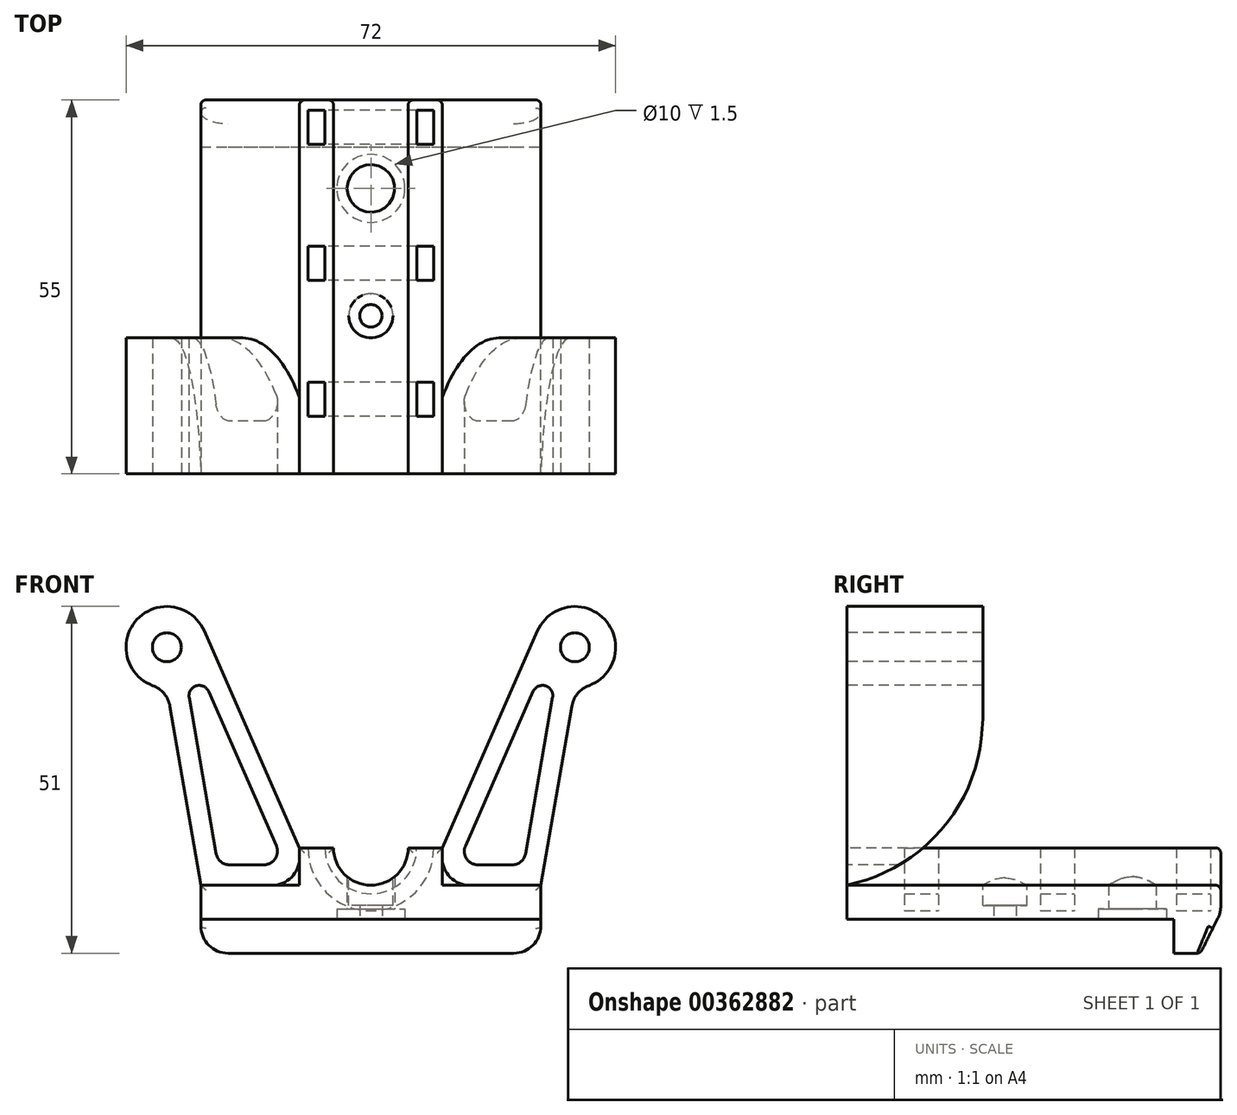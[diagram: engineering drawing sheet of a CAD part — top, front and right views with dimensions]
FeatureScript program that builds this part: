
annotation { "Feature Type Name" : "Feature", "Feature Type Description" : "" }
export const myFeature = defineFeature(function(context is Context, id is Id, definition is map)
    precondition{}
    {
        {
            var Q0;
            Q0=qCreatedBy(makeId("Top.planeOp"),FACE);
            var sketch = newSketch(context, id + "F0", { "sketchPlane" : qUnion([Q0])});
            skCircle(sketch, "E0", {"center": v(0, 0) * mm, "radius": 3.5 * mm});
            skLineSegment(sketch, "E1", {"start": v(0, 0) * mm, "end": v(0, -18.75) * mm, "construction": true});
            skCircle(sketch, "E2", {"center": v(0, -18.75) * mm, "radius": 1.65 * mm});
            skLineSegment(sketch, "E3", {"start": v(0, 0) * mm, "end": v(0, 13) * mm, "construction": true});
            skLineSegment(sketch, "E4", {"start": v(0, 13) * mm, "end": v(-25, 13) * mm});
            skLineSegment(sketch, "E5", {"start": v(-25, 13) * mm, "end": v(-25, -42) * mm});
            skLineSegment(sketch, "E6", {"start": v(-25, -42) * mm, "end": v(25, -42) * mm});
            skLineSegment(sketch, "E7", {"start": v(25, -42) * mm, "end": v(25, 13) * mm});
            skLineSegment(sketch, "E8", {"start": v(25, 13) * mm, "end": v(0, 13) * mm});
            skSolve(sketch);
        }
        {
            var Q0;
            Q0 = qSketchRegion(id + "F0", true);
            extrude(context, id + "F1", {"entities" : qUnion([Q0]), "depth" : 5 * mm});
        }
        {
            var Q0;
            Q0=makeQuery(id+"F1.opExtrude","CAP_FACE",FACE,{"disambiguationData":[OSD([sQuery(id+"F0.wireOp",EDGE,"E0"),sQuery(id+"F0.wireOp",EDGE,"E2"),sQuery(id+"F0.wireOp",EDGE,"E4"),sQuery(id+"F0.wireOp",EDGE,"E5"),sQuery(id+"F0.wireOp",EDGE,"E6"),sQuery(id+"F0.wireOp",EDGE,"E7"),sQuery(id+"F0.wireOp",EDGE,"E8")])],"isStart":true});
            var sketch = newSketch(context, id + "F2", { "sketchPlane" : qUnion([Q0])});
            skLineSegment(sketch, "E9.bottom", {"start": v(-25, -13) * mm, "end": v(25, -13) * mm});
            skLineSegment(sketch, "E9.top", {"start": v(-25, -6.1) * mm, "end": v(25, -6.1) * mm});
            skLineSegment(sketch, "E9.left", {"start": v(-25, -13) * mm, "end": v(-25, -6.1) * mm});
            skLineSegment(sketch, "E9.right", {"start": v(25, -13) * mm, "end": v(25, -6.1) * mm});
            skSolve(sketch);
        }
        {
            var Q0;
            Q0 = qSketchRegion(id + "F2", true);
            extrude(context, id + "F3", {"entities" : qUnion([Q0]), "operationType" : NewBodyOperationType.ADD, "depth" : 5 * mm});
        }
        {
            var Q0;
            Q0=makeQuery(id+"F1.opExtrude","CAP_FACE",FACE,{"disambiguationData":[OSD([sQuery(id+"F0.wireOp",EDGE,"E0"),sQuery(id+"F0.wireOp",EDGE,"E2"),sQuery(id+"F0.wireOp",EDGE,"E4"),sQuery(id+"F0.wireOp",EDGE,"E5"),sQuery(id+"F0.wireOp",EDGE,"E6"),sQuery(id+"F0.wireOp",EDGE,"E7"),sQuery(id+"F0.wireOp",EDGE,"E8")])],"isStart":true});
            var sketch = newSketch(context, id + "F4", { "sketchPlane" : qUnion([Q0])});
            skCircle(sketch, "E10", {"center": v(0, 0) * mm, "radius": 5 * mm});
            skSolve(sketch);
        }
        {
            var Q0;
            Q0 = qSketchRegion(id + "F4", true);
            extrude(context, id + "F5", {"entities" : qUnion([Q0]), "operationType" : NewBodyOperationType.REMOVE, "oppositeDirection" : true, "depth" : 1.5 * mm});
        }
        {
            var Q0;
            Q0=makeQuery(id+"F1.opExtrude","CAP_FACE",FACE,{"disambiguationData":[OSD([sQuery(id+"F0.wireOp",EDGE,"E0"),sQuery(id+"F0.wireOp",EDGE,"E2"),sQuery(id+"F0.wireOp",EDGE,"E4"),sQuery(id+"F0.wireOp",EDGE,"E5"),sQuery(id+"F0.wireOp",EDGE,"E6"),sQuery(id+"F0.wireOp",EDGE,"E7"),sQuery(id+"F0.wireOp",EDGE,"E8")])],"isStart":false});
            var sketch = newSketch(context, id + "F6", { "sketchPlane" : qUnion([Q0])});
            skCircle(sketch, "E11", {"center": v(0, -18.75) * mm, "radius": 3.25 * mm});
            skSolve(sketch);
        }
        {
            var Q0;
            Q0 = qSketchRegion(id + "F6", true);
            extrude(context, id + "F7", {"entities" : qUnion([Q0]), "operationType" : NewBodyOperationType.REMOVE, "oppositeDirection" : true, "depth" : 3 * mm});
        }
        {
            var Q0;
            Q0=makeQuery(id+"F3.opExtrude","CAP_EDGE",EDGE,{"disambiguationData":[OSD([sQuery(id+"F2.wireOp",EDGE,"E9.bottom")])],"isStart":false});
            chamfer(context, id + "F8", {"entities" : qUnion([Q0]), "chamferType" : ChamferType.TWO_OFFSETS, "width1" : 6 * mm, "oppositeDirection" : false, "width2" : 3 * mm, "tangentPropagation" : true});
        }
        {
            var Q0;
            Q0=makeQuery(id+"F1.opExtrude","SWEPT_FACE",FACE,{"disambiguationData":[OSD([sQuery(id+"F0.wireOp",EDGE,"E6")])]});
            var sketch = newSketch(context, id + "F9", { "sketchPlane" : qUnion([Q0])});
            skLineSegment(sketch, "E12", {"start": v(0, 0) * mm, "end": v(0, 10.5) * mm, "construction": true});
            skPoint(sketch, "E12.endSnap0", {"position": v(0, 5) * mm});
            skArc(sketch, "E13", {"start": v(-5.5, 10.5) * mm, "mid": v(0, 5) * mm, "end": v(5.5, 10.5) * mm});
            skLineSegment(sketch, "E14", {"start": v(-5.5, 10.5) * mm, "end": v(-10.5, 10.5) * mm});
            skLineSegment(sketch, "E15", {"start": v(-10.5, 10.5) * mm, "end": v(-10.5, 4.5) * mm});
            skLineSegment(sketch, "E16", {"start": v(5.5, 10.5) * mm, "end": v(10.5, 10.5) * mm});
            skLineSegment(sketch, "E17", {"start": v(10.5, 10.5) * mm, "end": v(10.5, 4.5) * mm});
            skLineSegment(sketch, "E18", {"start": v(10.5, 4.5) * mm, "end": v(-10.5, 4.5) * mm});
            skSolve(sketch);
        }
        {
            var Q0;
            Q0 = qSketchRegion(id + "F9", true);
            extrude(context, id + "F10", {"entities" : qUnion([Q0]), "operationType" : NewBodyOperationType.ADD, "oppositeDirection" : true, "depth" : 55 * mm});
        }
        {
            var Q0;
            Q0=makeQuery(id+"F10.boolean.opBoolean","MERGE",FACE,{"derivedFrom":[makeQuery(id+"F1.opExtrude","SWEPT_FACE",FACE,{"disambiguationData":[OSD([sQuery(id+"F0.wireOp",EDGE,"E6")])]}),makeQuery(id+"F10.opExtrude","CAP_FACE",FACE,{"disambiguationData":[OSD([sQuery(id+"F9.wireOp",EDGE,"E13"),sQuery(id+"F9.wireOp",EDGE,"E14"),sQuery(id+"F9.wireOp",EDGE,"E15"),sQuery(id+"F9.wireOp",EDGE,"E16"),sQuery(id+"F9.wireOp",EDGE,"E17"),sQuery(id+"F9.wireOp",EDGE,"E18")])],"isStart":true})]});
            var sketch = newSketch(context, id + "F11", { "sketchPlane" : qUnion([Q0])});
            skLineSegment(sketch, "E19", {"start": v(0, 0) * mm, "end": v(0, 40) * mm, "construction": true});
            skPoint(sketch, "E19.endSnap0", {"position": v(0, 5) * mm});
            skLineSegment(sketch, "E20", {"start": v(0, 40) * mm, "end": v(-30, 40) * mm, "construction": true});
            skLineSegment(sketch, "E21", {"start": v(0, 40) * mm, "end": v(30, 40) * mm, "construction": true});
            skCircle(sketch, "E22", {"center": v(-30, 40) * mm, "radius": 2.12 * mm});
            skCircle(sketch, "E23", {"center": v(30, 40) * mm, "radius": 2.12 * mm});
            skArc(sketch, "E24", {"start": v(-24.5, 42.41) * mm, "mid": v(-35.02, 43.28) * mm, "end": v(-30, 34) * mm});
            skArc(sketch, "E25", {"start": v(30, 34) * mm, "mid": v(35.02, 43.28) * mm, "end": v(24.5, 42.41) * mm});
            skLineSegment(sketch, "E26", {"start": v(-30, 34) * mm, "end": v(-25, 5) * mm});
            skLineSegment(sketch, "E27", {"start": v(-10.5, 10.5) * mm, "end": v(-24.5, 42.41) * mm});
            skLineSegment(sketch, "E28", {"start": v(-25, 5) * mm, "end": v(-10.5, 5) * mm});
            skLineSegment(sketch, "E29", {"start": v(-10.5, 5) * mm, "end": v(-10.5, 10.5) * mm});
            skLineSegment(sketch, "E30.0", {"start": v(-13.9, 10.8) * mm, "end": v(-23.87, 33.5) * mm});
            skLineSegment(sketch, "E30.1", {"start": v(-20.79, 8) * mm, "end": v(-15.74, 8) * mm});
            skLineSegment(sketch, "E30.2", {"start": v(-26.72, 32.64) * mm, "end": v(-22.76, 9.66) * mm});
            skPoint(sketch, "E31.visualSharp", {"position": v(-22.47, 8) * mm});
            skArc(sketch, "E31.filletArc", {"start": v(-22.76, 9.66) * mm, "mid": v(-22.08, 8.47) * mm, "end": v(-20.79, 8) * mm});
            skPoint(sketch, "E32.visualSharp", {"position": v(-12.68, 8) * mm});
            skArc(sketch, "E32.filletArc", {"start": v(-15.74, 8) * mm, "mid": v(-14.07, 8.9) * mm, "end": v(-13.9, 10.8) * mm});
            skPoint(sketch, "E33.visualSharp", {"position": v(-28.8, 44.75) * mm});
            skArc(sketch, "E33.filletArc", {"start": v(-23.87, 33.5) * mm, "mid": v(-25.67, 34.33) * mm, "end": v(-26.72, 32.64) * mm});
            skLineSegment(sketch, "E34.MirrorCS", {"start": v(13.9, 10.8) * mm, "end": v(23.87, 33.5) * mm});
            skLineSegment(sketch, "E35.MirrorCS", {"start": v(10.5, 10.5) * mm, "end": v(24.5, 42.41) * mm});
            skLineSegment(sketch, "E36.MirrorCS", {"start": v(10.5, 5) * mm, "end": v(10.5, 10.5) * mm});
            skLineSegment(sketch, "E37.MirrorCS", {"start": v(25, 5) * mm, "end": v(10.5, 5) * mm});
            skLineSegment(sketch, "E38.MirrorCS", {"start": v(30, 34) * mm, "end": v(25, 5) * mm});
            skArc(sketch, "E39.MirrorCS", {"start": v(15.74, 8) * mm, "mid": v(14.07, 8.9) * mm, "end": v(13.9, 10.8) * mm});
            skLineSegment(sketch, "E40.MirrorCS", {"start": v(20.79, 8) * mm, "end": v(15.74, 8) * mm});
            skArc(sketch, "E41.MirrorCS", {"start": v(22.76, 9.66) * mm, "mid": v(22.08, 8.47) * mm, "end": v(20.79, 8) * mm});
            skLineSegment(sketch, "E42.MirrorCS", {"start": v(26.72, 32.64) * mm, "end": v(22.76, 9.66) * mm});
            skArc(sketch, "E43.MirrorCS", {"start": v(23.87, 33.5) * mm, "mid": v(25.67, 34.33) * mm, "end": v(26.72, 32.64) * mm});
            skSolve(sketch);
        }
        {
            var Q0;
            Q0=makeQuery(id+"F10.opExtrude","SWEPT_FACE",FACE,{"disambiguationData":[OSD([sQuery(id+"F9.wireOp",EDGE,"E16")])]});
            var sketch = newSketch(context, id + "F12", { "sketchPlane" : qUnion([Q0])});
            skLineSegment(sketch, "E44", {"start": v(0, 0) * mm, "end": v(0, 13) * mm, "construction": true});
            skLineSegment(sketch, "E45", {"start": v(0, 13) * mm, "end": v(8, 13) * mm, "construction": true});
            skLineSegment(sketch, "E46", {"start": v(8, 13) * mm, "end": v(8, -42) * mm, "construction": true});
            skLineSegment(sketch, "E47.bottom", {"start": v(9.25, -33.5) * mm, "end": v(6.75, -33.5) * mm});
            skLineSegment(sketch, "E47.top", {"start": v(9.25, -28.5) * mm, "end": v(6.75, -28.5) * mm});
            skLineSegment(sketch, "E47.left", {"start": v(9.25, -33.5) * mm, "end": v(9.25, -28.5) * mm});
            skLineSegment(sketch, "E47.right", {"start": v(6.75, -33.5) * mm, "end": v(6.75, -28.5) * mm});
            skPoint(sketch, "E47.middle", {"position": v(8, -31) * mm});
            skLineSegment(sketch, "E48.bottom", {"start": v(9.25, 6.5) * mm, "end": v(6.75, 6.5) * mm});
            skLineSegment(sketch, "E48.top", {"start": v(9.25, 11.5) * mm, "end": v(6.75, 11.5) * mm});
            skLineSegment(sketch, "E48.left", {"start": v(9.25, 6.5) * mm, "end": v(9.25, 11.5) * mm});
            skLineSegment(sketch, "E48.right", {"start": v(6.75, 6.5) * mm, "end": v(6.75, 11.5) * mm});
            skPoint(sketch, "E48.middle", {"position": v(8, 9) * mm});
            skLineSegment(sketch, "E49.bottom", {"start": v(9.25, -13.5) * mm, "end": v(6.75, -13.5) * mm});
            skLineSegment(sketch, "E49.top", {"start": v(9.25, -8.5) * mm, "end": v(6.75, -8.5) * mm});
            skLineSegment(sketch, "E49.left", {"start": v(9.25, -13.5) * mm, "end": v(9.25, -8.5) * mm});
            skLineSegment(sketch, "E49.right", {"start": v(6.75, -13.5) * mm, "end": v(6.75, -8.5) * mm});
            skPoint(sketch, "E49.middle", {"position": v(8, -11) * mm});
            skSolve(sketch);
        }
        {
            var Q0;
            Q0 = qSketchRegion(id + "F12", true);
            var Q1;
            Q1=sQuery(id+"F12.wireOp",EDGE,"E44");
            revolve(context, id + "F13", {"operationType" : NewBodyOperationType.REMOVE, "entities" : qUnion([Q0]), "axis" : qUnion([Q1]), "revolveType" : RevolveType.FULL, "oppositeDirection" : true});
        }
        {
            var Q0;
            Q0 = qSketchRegion(id + "F11", true);
            extrude(context, id + "F14", {"entities" : qUnion([Q0]), "oppositeDirection" : true, "depth" : 20 * mm});
        }
        {
            var Q0;
            Q0=makeQuery(id+"F10.boolean.opBoolean","INTERSECT",EDGE,{"derivedFrom":[makeQuery(id+"F1.opExtrude","CAP_FACE",FACE,{"disambiguationData":[OSD([sQuery(id+"F0.wireOp",EDGE,"E0"),sQuery(id+"F0.wireOp",EDGE,"E2"),sQuery(id+"F0.wireOp",EDGE,"E4"),sQuery(id+"F0.wireOp",EDGE,"E5"),sQuery(id+"F0.wireOp",EDGE,"E6"),sQuery(id+"F0.wireOp",EDGE,"E7"),sQuery(id+"F0.wireOp",EDGE,"E8")])],"isStart":false}),makeQuery(id+"F10.opExtrude","SWEPT_FACE",FACE,{"disambiguationData":[OSD([sQuery(id+"F9.wireOp",EDGE,"E15")])]})]});
            var Q1;
            Q1=makeQuery(id+"F10.boolean.opBoolean","INTERSECT",EDGE,{"derivedFrom":[makeQuery(id+"F1.opExtrude","CAP_FACE",FACE,{"disambiguationData":[OSD([sQuery(id+"F0.wireOp",EDGE,"E0"),sQuery(id+"F0.wireOp",EDGE,"E2"),sQuery(id+"F0.wireOp",EDGE,"E4"),sQuery(id+"F0.wireOp",EDGE,"E5"),sQuery(id+"F0.wireOp",EDGE,"E6"),sQuery(id+"F0.wireOp",EDGE,"E7"),sQuery(id+"F0.wireOp",EDGE,"E8")])],"isStart":false}),makeQuery(id+"F10.opExtrude","SWEPT_FACE",FACE,{"disambiguationData":[OSD([sQuery(id+"F9.wireOp",EDGE,"E17")])]})]});
            var Q2;
            Q2=makeQuery(id+"F3.opExtrude","CAP_EDGE",EDGE,{"disambiguationData":[OSD([sQuery(id+"F2.wireOp",EDGE,"E9.right")])],"isStart":false});
            var Q3;
            Q3=makeQuery(id+"F3.opExtrude","CAP_EDGE",EDGE,{"disambiguationData":[OSD([sQuery(id+"F2.wireOp",EDGE,"E9.left")])],"isStart":false});
            var Q4;
            {var subQ0=sQuery(id+"F2.wireOp",EDGE,"E9.bottom");Q4=makeQuery(id+"F8.opChamfer","BLEND_EDGE",EDGE,{"blendedFrom":[makeQuery(id+"F3.opExtrude","CAP_EDGE",EDGE,{"disambiguationData":[OSD([subQ0])],"isStart":false}),makeQuery(id+"F3.boolean.opBoolean","MERGE",FACE,{"derivedFrom":[makeQuery(id+"F1.opExtrude","SWEPT_FACE",FACE,{"disambiguationData":[OSD([sQuery(id+"F0.wireOp",EDGE,"E4"),sQuery(id+"F0.wireOp",EDGE,"E8")])]}),makeQuery(id+"F3.opExtrude","SWEPT_FACE",FACE,{"disambiguationData":[OSD([subQ0])]})]})],"blendedInto":[makeQuery(id+"F3.boolean.opBoolean","MERGE",FACE,{"derivedFrom":[makeQuery(id+"F1.opExtrude","SWEPT_FACE",FACE,{"disambiguationData":[OSD([sQuery(id+"F0.wireOp",EDGE,"E4"),sQuery(id+"F0.wireOp",EDGE,"E8")])]}),makeQuery(id+"F3.opExtrude","SWEPT_FACE",FACE,{"disambiguationData":[OSD([subQ0])]})]})]});}
            var Q5;
            Q5=makeQuery(id+"F14.opExtrude","SWEPT_EDGE",EDGE,{"disambiguationData":[OSD([sQuery(id+"F11.wireOp",EDGE,"E25"),sQuery(id+"F11.wireOp",EDGE,"E38.MirrorCS")])]});
            var Q6;
            Q6=makeQuery(id+"F14.opExtrude","SWEPT_EDGE",EDGE,{"disambiguationData":[OSD([sQuery(id+"F11.wireOp",EDGE,"E24"),sQuery(id+"F11.wireOp",EDGE,"E26")])]});
            fillet(context, id + "F15", {"entities" : qUnion([Q0, Q1, Q2, Q3, Q4, Q5, Q6]), "radius" : 4 * mm, "tangentPropagation" : true, "allowEdgeOverflow" : false});
        }
        {
            var Q0;
            Q0=makeQuery(id+"F14.opExtrude","CAP_EDGE",EDGE,{"disambiguationData":[OSD([sQuery(id+"F11.wireOp",EDGE,"E28")])],"isStart":false});
            var Q1;
            Q1=makeQuery(id+"F14.opExtrude","CAP_EDGE",EDGE,{"disambiguationData":[OSD([sQuery(id+"F11.wireOp",EDGE,"E37.MirrorCS")])],"isStart":false});
            fillet(context, id + "F16", {"entities" : qUnion([Q0, Q1]), "radius" : 25 * mm, "tangentPropagation" : true, "allowEdgeOverflow" : false});
        }
        {
            var Q0;
            Q0=makeQuery(id+"F10.opExtrude","CAP_EDGE",EDGE,{"disambiguationData":[OSD([sQuery(id+"F9.wireOp",EDGE,"E14")])],"isStart":false});
            var Q1;
            Q1=makeQuery(id+"F10.opExtrude","CAP_EDGE",EDGE,{"disambiguationData":[OSD([sQuery(id+"F9.wireOp",EDGE,"E13")])],"isStart":false});
            var Q2;
            Q2=makeQuery(id+"F10.opExtrude","CAP_EDGE",EDGE,{"disambiguationData":[OSD([sQuery(id+"F9.wireOp",EDGE,"E16")])],"isStart":false});
            var Q3;
            {var subQ0=sQuery(id+"F9.wireOp",EDGE,"E17");var subQ1=sQuery(id+"F0.wireOp",EDGE,"E8");var subQ2=sQuery(id+"F0.wireOp",EDGE,"E4");Q3=makeQuery(id+"F15.opFillet","BLEND_EDGE",EDGE,{"blendedFrom":[makeQuery(id+"F10.boolean.opBoolean","INTERSECT",EDGE,{"derivedFrom":[makeQuery(id+"F1.opExtrude","CAP_FACE",FACE,{"disambiguationData":[OSD([sQuery(id+"F0.wireOp",EDGE,"E0"),sQuery(id+"F0.wireOp",EDGE,"E2"),subQ2,sQuery(id+"F0.wireOp",EDGE,"E5"),sQuery(id+"F0.wireOp",EDGE,"E6"),sQuery(id+"F0.wireOp",EDGE,"E7"),subQ1])],"isStart":false}),makeQuery(id+"F10.opExtrude","SWEPT_FACE",FACE,{"disambiguationData":[OSD([subQ0])]})]}),makeQuery(id+"F10.boolean.opBoolean","MERGE",FACE,{"derivedFrom":[makeQuery(id+"F3.boolean.opBoolean","MERGE",FACE,{"derivedFrom":[makeQuery(id+"F1.opExtrude","SWEPT_FACE",FACE,{"disambiguationData":[OSD([subQ2,subQ1])]}),makeQuery(id+"F3.opExtrude","SWEPT_FACE",FACE,{"disambiguationData":[OSD([sQuery(id+"F2.wireOp",EDGE,"E9.bottom")])]})]}),makeQuery(id+"F10.opExtrude","CAP_FACE",FACE,{"disambiguationData":[OSD([sQuery(id+"F9.wireOp",EDGE,"E13"),sQuery(id+"F9.wireOp",EDGE,"E14"),sQuery(id+"F9.wireOp",EDGE,"E15"),sQuery(id+"F9.wireOp",EDGE,"E16"),subQ0,sQuery(id+"F9.wireOp",EDGE,"E18")])],"isStart":false})]})],"blendedInto":[makeQuery(id+"F10.boolean.opBoolean","MERGE",FACE,{"derivedFrom":[makeQuery(id+"F3.boolean.opBoolean","MERGE",FACE,{"derivedFrom":[makeQuery(id+"F1.opExtrude","SWEPT_FACE",FACE,{"disambiguationData":[OSD([subQ2,subQ1])]}),makeQuery(id+"F3.opExtrude","SWEPT_FACE",FACE,{"disambiguationData":[OSD([sQuery(id+"F2.wireOp",EDGE,"E9.bottom")])]})]}),makeQuery(id+"F10.opExtrude","CAP_FACE",FACE,{"disambiguationData":[OSD([sQuery(id+"F9.wireOp",EDGE,"E13"),sQuery(id+"F9.wireOp",EDGE,"E14"),sQuery(id+"F9.wireOp",EDGE,"E15"),sQuery(id+"F9.wireOp",EDGE,"E16"),subQ0,sQuery(id+"F9.wireOp",EDGE,"E18")])],"isStart":false})]})]});}
            var Q4;
            {var subQ0=sQuery(id+"F9.wireOp",EDGE,"E15");var subQ1=sQuery(id+"F0.wireOp",EDGE,"E8");var subQ2=sQuery(id+"F0.wireOp",EDGE,"E4");Q4=makeQuery(id+"F15.opFillet","BLEND_EDGE",EDGE,{"blendedFrom":[makeQuery(id+"F10.boolean.opBoolean","INTERSECT",EDGE,{"derivedFrom":[makeQuery(id+"F1.opExtrude","CAP_FACE",FACE,{"disambiguationData":[OSD([sQuery(id+"F0.wireOp",EDGE,"E0"),sQuery(id+"F0.wireOp",EDGE,"E2"),subQ2,sQuery(id+"F0.wireOp",EDGE,"E5"),sQuery(id+"F0.wireOp",EDGE,"E6"),sQuery(id+"F0.wireOp",EDGE,"E7"),subQ1])],"isStart":false}),makeQuery(id+"F10.opExtrude","SWEPT_FACE",FACE,{"disambiguationData":[OSD([subQ0])]})]}),makeQuery(id+"F10.boolean.opBoolean","MERGE",FACE,{"derivedFrom":[makeQuery(id+"F3.boolean.opBoolean","MERGE",FACE,{"derivedFrom":[makeQuery(id+"F1.opExtrude","SWEPT_FACE",FACE,{"disambiguationData":[OSD([subQ2,subQ1])]}),makeQuery(id+"F3.opExtrude","SWEPT_FACE",FACE,{"disambiguationData":[OSD([sQuery(id+"F2.wireOp",EDGE,"E9.bottom")])]})]}),makeQuery(id+"F10.opExtrude","CAP_FACE",FACE,{"disambiguationData":[OSD([sQuery(id+"F9.wireOp",EDGE,"E13"),sQuery(id+"F9.wireOp",EDGE,"E14"),subQ0,sQuery(id+"F9.wireOp",EDGE,"E16"),sQuery(id+"F9.wireOp",EDGE,"E17"),sQuery(id+"F9.wireOp",EDGE,"E18")])],"isStart":false})]})],"blendedInto":[makeQuery(id+"F10.boolean.opBoolean","MERGE",FACE,{"derivedFrom":[makeQuery(id+"F3.boolean.opBoolean","MERGE",FACE,{"derivedFrom":[makeQuery(id+"F1.opExtrude","SWEPT_FACE",FACE,{"disambiguationData":[OSD([subQ2,subQ1])]}),makeQuery(id+"F3.opExtrude","SWEPT_FACE",FACE,{"disambiguationData":[OSD([sQuery(id+"F2.wireOp",EDGE,"E9.bottom")])]})]}),makeQuery(id+"F10.opExtrude","CAP_FACE",FACE,{"disambiguationData":[OSD([sQuery(id+"F9.wireOp",EDGE,"E13"),sQuery(id+"F9.wireOp",EDGE,"E14"),subQ0,sQuery(id+"F9.wireOp",EDGE,"E16"),sQuery(id+"F9.wireOp",EDGE,"E17"),sQuery(id+"F9.wireOp",EDGE,"E18")])],"isStart":false})]})]});}
            var Q5;
            Q5=makeQuery(id+"F10.opExtrude","CAP_EDGE",EDGE,{"disambiguationData":[OSD([sQuery(id+"F9.wireOp",EDGE,"E15")])],"isStart":false});
            var Q6;
            Q6=makeQuery(id+"F10.opExtrude","CAP_EDGE",EDGE,{"disambiguationData":[OSD([sQuery(id+"F9.wireOp",EDGE,"E17")])],"isStart":false});
            var Q7;
            {var subQ0=sQuery(id+"F0.wireOp",EDGE,"E8");var subQ1=sQuery(id+"F0.wireOp",EDGE,"E4");var subQ3=sQuery(id+"F0.wireOp",EDGE,"E7");Q7=makeQuery(id+"F10.boolean.opBoolean","SPLIT",EDGE,{"disambiguationData":[TD([makeQuery(id+"F1.opExtrude","SWEPT_FACE",FACE,{"disambiguationData":[OSD([subQ3])]})])],"derivedFrom":makeQuery(id+"F1.opExtrude","CAP_EDGE",EDGE,{"disambiguationData":[OSD([subQ1,subQ0])],"isStart":false})});}
            var Q8;
            Q8=makeQuery(id+"F3.boolean.opBoolean","MERGE",EDGE,{"derivedFrom":[makeQuery(id+"F1.opExtrude","SWEPT_EDGE",EDGE,{"disambiguationData":[OSD([sQuery(id+"F0.wireOp",EDGE,"E7"),sQuery(id+"F0.wireOp",EDGE,"E8")])]}),makeQuery(id+"F3.opExtrude","SWEPT_EDGE",EDGE,{"disambiguationData":[OSD([sQuery(id+"F2.wireOp",EDGE,"E9.bottom"),sQuery(id+"F2.wireOp",EDGE,"E9.right")])]})]});
            fillet(context, id + "F17", {"entities" : qUnion([Q0, Q1, Q2, Q3, Q4, Q5, Q6, Q7, Q8]), "radius" : 0.75 * mm, "tangentPropagation" : true, "allowEdgeOverflow" : false});
        }
        {
            var Q0;
            Q0=makeQuery(id+"F1.opExtrude","CAP_FACE",FACE,{"disambiguationData":[OSD([sQuery(id+"F0.wireOp",EDGE,"E0"),sQuery(id+"F0.wireOp",EDGE,"E2"),sQuery(id+"F0.wireOp",EDGE,"E4"),sQuery(id+"F0.wireOp",EDGE,"E5"),sQuery(id+"F0.wireOp",EDGE,"E6"),sQuery(id+"F0.wireOp",EDGE,"E7"),sQuery(id+"F0.wireOp",EDGE,"E8")])],"isStart":true});
            var sketch = newSketch(context, id + "F18", { "sketchPlane" : qUnion([Q0])});
            skCircle(sketch, "E50", {"center": v(0, 0) * mm, "radius": 3.5 * mm});
            skCircle(sketch, "E51", {"center": v(0, 18.75) * mm, "radius": 1.65 * mm});
            skSolve(sketch);
        }
        {
            var Q0;
            Q0 = qSketchRegion(id + "F18", true);
            extrude(context, id + "F19", {"entities" : qUnion([Q0]), "operationType" : NewBodyOperationType.REMOVE, "endBound" : BoundingType.THROUGH_ALL, "oppositeDirection" : true, "depth" : 25 * mm});
        }
        {
            var Q0;
            Q0=makeQuery(id+"F7.boolean.opBoolean","COPY",FACE,{"derivedFrom":makeQuery(id+"F7.opExtrude","CAP_FACE",FACE,{"disambiguationData":[OSD([sQuery(id+"F6.wireOp",EDGE,"E11")])],"isStart":false})});
            var sketch = newSketch(context, id + "F20", { "sketchPlane" : qUnion([Q0])});
            skCircle(sketch, "E52", {"center": v(0, -18.75) * mm, "radius": 3.25 * mm});
            skSolve(sketch);
        }
        {
            var Q0;
            Q0 = qSketchRegion(id + "F20", true);
            extrude(context, id + "F21", {"entities" : qUnion([Q0]), "operationType" : NewBodyOperationType.REMOVE, "depth" : 25 * mm});
        }
    });
